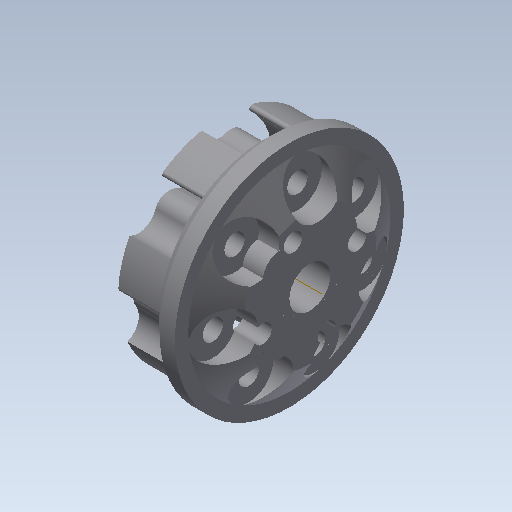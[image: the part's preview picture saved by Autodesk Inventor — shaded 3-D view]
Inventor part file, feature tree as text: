
AUTODESK INVENTOR PART (.ipt)
format: ipt  version: 2020 (Build 240168000, 168)  size: 650,752 bytes
history: native  units: in
note: dims shown in document units (in); Inventor stores cm internally (conversion verified against a paired STEP export)
features: other x4, sketch x4, extrude x2, plane x2
ambient origin geometry x8: Origin, YZ Plane, XZ Plane, XY Plane, X Axis, Y Axis, Z Axis, Center Point
bodies: Solid1 (feature_tree)
feature tree (12):
  other  "Mecanum Adaptor 1.3.ipt"
  extrude  "Extrusion1"  Depth=0.217in TaperAngle=0.0deg
  extrude  "Extrusion2"  Depth=0.1406in
  other  "Solid1::Mecanum Adaptor 1.3.ipt"
  other  "TaggingFeature1"
  sketch  "Sketch6"  dims[d0=0.3937in]
  sketch  "Sketch11"  dims[d4=0.4724in d5=0.0in d6=0.0787in d7=1.757in d8=1.6061in d9=0.0in d10=90.0deg d11=0.0in d12=90.0deg d13=0.1181in d14=0.0in d15=0.1575in d16=2.7559in d21=0.0in d23=0.0in d25=0.0in d26=0.1575in d27=0.0in d28=0.374in d29=2.7559in d33=0.0787in d34=0.0in d35=0.1378in d36=0.0in d38=0.0in d55=2.7559in d60=0.0in d61=0.2756in d62=0.7874in d64=0.446in d65=0.7874in d67=0.446in d70=0.0984in d71=0.0in d72=0.2638in d73=0.1575in d75=0.2638in d76=0.1575in d78=0.2638in d79=0.1575in d81=0.2638in d82=0.1575in d84=0.2638in d85=0.1575in d87=0.2638in d88=0.1575in d90=0.2638in d91=0.1575in d93=0.1575in d2=360.0deg d18=360.0deg d31=360.0deg d57=360.0deg d1=0.217in d3=0.0in]
  plane  "Work Plane1"
  plane  "Work Plane2"
  other  "Work Axis1"
  sketch  "Sketch18"  dims[d19=0.1406in d20=0.1406in]
  sketch  "Sketch19"  dims[d22=0.1406in d24=0.1406in d30=0.7795in d32=0.0in]
